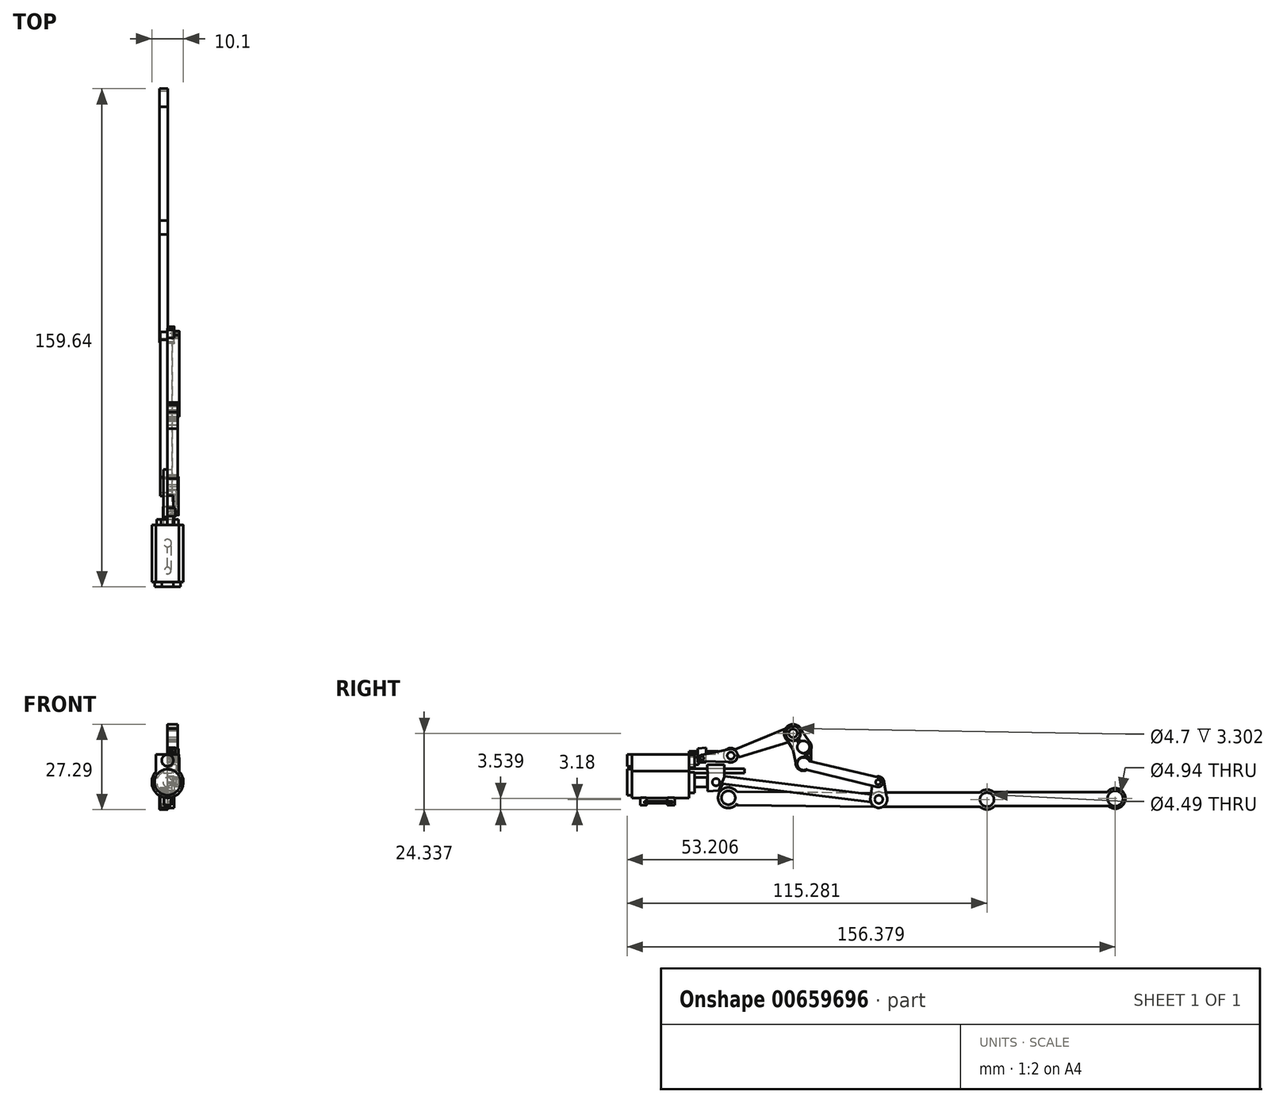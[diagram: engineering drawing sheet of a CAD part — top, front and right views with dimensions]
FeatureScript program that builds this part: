
annotation { "Feature Type Name" : "Feature", "Feature Type Description" : "" }
export const myFeature = defineFeature(function(context is Context, id is Id, definition is map)
    precondition{}
    {
        {
            var Q0;
            Q0=qCreatedBy(makeId("Front.planeOp"),FACE);
            var sketch = newSketch(context, id + "F0", { "sketchPlane" : qUnion([Q0])});
            skCircle(sketch, "E0", {"center": v(0, 0) * mm, "radius": 5.05 * mm});
            skLineSegment(sketch, "E1.bottom", {"start": v(-3.69, 8.87) * mm, "end": v(3.58, 8.87) * mm});
            skLineSegment(sketch, "E1.top", {"start": v(-3.69, 3.57) * mm, "end": v(3.58, 3.57) * mm});
            skLineSegment(sketch, "E1.left", {"start": v(-3.69, 8.87) * mm, "end": v(-3.69, 3.57) * mm});
            skLineSegment(sketch, "E1.right", {"start": v(3.58, 8.87) * mm, "end": v(3.58, 3.57) * mm});
            skSolve(sketch);
        }
        {
            var Q0;
            Q0=qSketchRegion(id+"F0",true);
            extrude(context, id + "F1", {"entities" : qUnion([Q0]), "depth" : 18.29 * mm, "offsetDistance" : 25.4 * mm});
        }
        {
            var Q0;
            Q0=qCreatedBy(makeId("Front.planeOp"),FACE);
            var sketch = newSketch(context, id + "F2", { "sketchPlane" : qUnion([Q0])});
            skCircle(sketch, "E2", {"center": v(0, 0) * mm, "radius": 3.48 * mm});
            skCircle(sketch, "E3", {"center": v(0, 6.69) * mm, "radius": 2.05 * mm});
            skSolve(sketch);
        }
        {
            var Q0;
            Q0=qSketchRegion(id+"F2",true);
            extrude(context, id + "F3", {"entities" : qUnion([Q0]), "operationType" : NewBodyOperationType.ADD, "oppositeDirection" : true, "depth" : 1.78 * mm, "offsetDistance" : 25.4 * mm});
        }
        {
            var Q0;
            Q0=qCreatedBy(makeId("Front.planeOp"),FACE);
            var sketch = newSketch(context, id + "F4", { "sketchPlane" : qUnion([Q0])});
            skCircle(sketch, "E4", {"center": v(0, 0) * mm, "radius": 4.19 * mm});
            skCircle(sketch, "E5", {"center": v(0, 6.96) * mm, "radius": 1.86 * mm});
            skSolve(sketch);
        }
        {
            var Q0;
            Q0=qSketchRegion(id+"F4",true);
            extrude(context, id + "F5", {"entities" : qUnion([Q0]), "operationType" : NewBodyOperationType.ADD, "depth" : 19.8 * mm, "offsetDistance" : 25.4 * mm});
        }
        {
            var Q0;
            Q0=qCreatedBy(makeId("Top.planeOp"),FACE);
            var sketch = newSketch(context, id + "F6", { "sketchPlane" : qUnion([Q0])});
            skCircle(sketch, "E6", {"center": v(0, -14.6) * mm, "radius": 1.06 * mm});
            skCircle(sketch, "E7", {"center": v(0, -5.8) * mm, "radius": 1.24 * mm});
            skSolve(sketch);
        }
        {
            var Q0;
            Q0=qSketchRegion(id+"F6",true);
            extrude(context, id + "F7", {"entities" : qUnion([Q0]), "operationType" : NewBodyOperationType.ADD, "oppositeDirection" : true, "depth" : 7.37 * mm, "offsetDistance" : 25.4 * mm});
        }
        {
            var Q0;
            Q0=qCreatedBy(makeId("Right.planeOp"),FACE);
            var sketch = newSketch(context, id + "F8", { "sketchPlane" : qUnion([Q0])});
            skLineSegment(sketch, "E8.bottom", {"start": v(-14.36, -6.78) * mm, "end": v(-5.2, -6.78) * mm});
            skLineSegment(sketch, "E8.top", {"start": v(-14.36, -6.08) * mm, "end": v(-5.2, -6.08) * mm});
            skLineSegment(sketch, "E8.left", {"start": v(-14.36, -6.78) * mm, "end": v(-14.36, -6.08) * mm});
            skLineSegment(sketch, "E8.right", {"start": v(-5.2, -6.78) * mm, "end": v(-5.2, -6.08) * mm});
            skSolve(sketch);
        }
        {
            var Q0;
            Q0=qSketchRegion(id+"F8",true);
            extrude(context, id + "F9", {"entities" : qUnion([Q0]), "operationType" : NewBodyOperationType.ADD, "depth" : 1.27 * mm, "offsetDistance" : 25.4 * mm});
        }
        {
            var Q0;
            Q0=qCreatedBy(makeId("Front.planeOp"),FACE);
            var sketch = newSketch(context, id + "F10", { "sketchPlane" : qUnion([Q0])});
            skLineSegment(sketch, "E9.bottom", {"start": v(-1.32, 4.33) * mm, "end": v(1.32, 4.33) * mm});
            skLineSegment(sketch, "E9.top", {"start": v(-1.32, 2.91) * mm, "end": v(1.32, 2.91) * mm});
            skLineSegment(sketch, "E9.left", {"start": v(-1.32, 4.33) * mm, "end": v(-1.32, 2.91) * mm});
            skLineSegment(sketch, "E9.right", {"start": v(1.32, 4.33) * mm, "end": v(1.32, 2.91) * mm});
            skPoint(sketch, "E9.middle", {"position": v(0, 3.62) * mm});
            skSolve(sketch);
        }
        {
            var Q0;
            Q0=qSketchRegion(id+"F10",true);
            extrude(context, id + "F11", {"entities" : qUnion([Q0]), "operationType" : NewBodyOperationType.ADD, "oppositeDirection" : true, "depth" : 17.78 * mm, "offsetDistance" : 25.4 * mm});
        }
        {
            var Q0;
            Q0=qCreatedBy(makeId("Right.planeOp"),FACE);
            var sketch = newSketch(context, id + "F12", { "sketchPlane" : qUnion([Q0])});
            skLineSegment(sketch, "E10", {"start": v(5.85, 5.6) * mm, "end": v(11.32, 5.6) * mm});
            skLineSegment(sketch, "E11", {"start": v(11.32, 5.6) * mm, "end": v(11.32, 1.7) * mm});
            skLineSegment(sketch, "E12", {"start": v(11.32, 1.7) * mm, "end": v(6.02, 1.7) * mm});
            skLineSegment(sketch, "E13", {"start": v(6.02, 1.7) * mm, "end": v(5.85, 5.6) * mm});
            skLineSegment(sketch, "E14", {"start": v(6.02, 1.7) * mm, "end": v(6.02, -2.89) * mm});
            skLineSegment(sketch, "E15", {"start": v(11.32, 1.7) * mm, "end": v(9.55, -2.71) * mm});
            skLineSegment(sketch, "E16", {"start": v(9.55, -2.71) * mm, "end": v(6.02, -2.89) * mm});
            skCircle(sketch, "E17", {"center": v(8.67, 0) * mm, "radius": 1.18 * mm});
            skPoint(sketch, "E17.centerSnap0", {"position": v(8.67, 1.7) * mm});
            skSolve(sketch);
        }
        {
            var Q0;
            Q0=qSketchRegion(id+"F12",true);
            extrude(context, id + "F13", {"entities" : qUnion([Q0]), "operationType" : NewBodyOperationType.ADD, "depth" : 2.8 * mm, "offsetDistance" : 25.4 * mm});
        }
        {
            var Q0;
            Q0=qCreatedBy(makeId("Front.planeOp"),FACE);
            var sketch = newSketch(context, id + "F14", { "sketchPlane" : qUnion([Q0])});
            skCircle(sketch, "E18", {"center": v(0, 0) * mm, "radius": 1.49 * mm});
            skSolve(sketch);
        }
        {
            var Q0;
            Q0=qSketchRegion(id+"F14",true);
            extrude(context, id + "F15", {"entities" : qUnion([Q0]), "operationType" : NewBodyOperationType.ADD, "oppositeDirection" : true, "depth" : 5.84 * mm, "offsetDistance" : 25.4 * mm});
        }
        {
            var Q0;
            Q0=qCreatedBy(makeId("Right.planeOp"),FACE);
            var sketch = newSketch(context, id + "F16", { "sketchPlane" : qUnion([Q0])});
            skCircle(sketch, "E19", {"center": v(8.62, 0) * mm, "radius": 2.28 * mm});
            skLineSegment(sketch, "E20", {"start": v(8.62, 2.28) * mm, "end": v(58.69, -3.97) * mm});
            skLineSegment(sketch, "E21", {"start": v(58.69, -3.97) * mm, "end": v(58.38, -6.43) * mm});
            skLineSegment(sketch, "E22", {"start": v(58.38, -6.43) * mm, "end": v(8.62, -0.22) * mm});
            skLineSegment(sketch, "E23", {"start": v(8.62, -0.22) * mm, "end": v(58.38, -6.43) * mm});
            skCircle(sketch, "E24", {"center": v(60.87, -5.6) * mm, "radius": 2.52 * mm});
            skSolve(sketch);
        }
        {
            var Q0;
            Q0=qSketchRegion(id+"F16",true);
            extrude(context, id + "F17", {"entities" : qUnion([Q0]), "operationType" : NewBodyOperationType.ADD, "depth" : 1.52 * mm, "offsetDistance" : 25.4 * mm});
        }
        {
            var Q0;
            Q0=qCreatedBy(makeId("Right.planeOp"),FACE);
            var sketch = newSketch(context, id + "F18", { "sketchPlane" : qUnion([Q0])});
            skCircle(sketch, "E25", {"center": v(60.8, -5.52) * mm, "radius": 2.72 * mm});
            skCircle(sketch, "E26", {"center": v(60.66, 0) * mm, "radius": 1.84 * mm});
            skLineSegment(sketch, "E27", {"start": v(58.82, 0) * mm, "end": v(58.19, -4.77) * mm});
            skLineSegment(sketch, "E28", {"start": v(62.5, 0) * mm, "end": v(63.25, -4.3) * mm});
            skCircle(sketch, "E29", {"center": v(60.66, 0) * mm, "radius": 1.1 * mm});
            skCircle(sketch, "E30", {"center": v(60.8, -5.52) * mm, "radius": 1.3 * mm});
            skSolve(sketch);
        }
        {
            var Q0;
            Q0=qSketchRegion(id+"F18",true);
            extrude(context, id + "F19", {"entities" : qUnion([Q0]), "operationType" : NewBodyOperationType.ADD, "depth" : 2.16 * mm, "offsetDistance" : 25.4 * mm});
        }
        {
            var Q0;
            Q0=qCreatedBy(makeId("Right.planeOp"),FACE);
            var sketch = newSketch(context, id + "F20", { "sketchPlane" : qUnion([Q0])});
            skCircle(sketch, "E31", {"center": v(60.6, 0) * mm, "radius": 1.56 * mm});
            skCircle(sketch, "E32", {"center": v(60.6, 0) * mm, "radius": 0.82 * mm});
            skLineSegment(sketch, "E33", {"start": v(61.05, 1.5) * mm, "end": v(38.5, 6.7) * mm});
            skLineSegment(sketch, "E34", {"start": v(60.3, -1.53) * mm, "end": v(37.9, 3.97) * mm});
            skLineSegment(sketch, "E35", {"start": v(37.9, 3.97) * mm, "end": v(38.5, 6.7) * mm});
            skCircle(sketch, "E36", {"center": v(36.73, 5.88) * mm, "radius": 2.03 * mm});
            skSolve(sketch);
        }
        {
            var Q0;
            Q0=qSketchRegion(id+"F20",true);
            extrude(context, id + "F21", {"entities" : qUnion([Q0]), "operationType" : NewBodyOperationType.ADD, "depth" : 3.7 * mm, "offsetDistance" : 25.4 * mm});
        }
        {
            var Q0;
            Q0=qCreatedBy(makeId("Right.planeOp"),FACE);
            var sketch = newSketch(context, id + "F22", { "sketchPlane" : qUnion([Q0])});
            skCircle(sketch, "E37", {"center": v(36.65, 6.15) * mm, "radius": 2.53 * mm});
            skCircle(sketch, "E38", {"center": v(36.65, 11.27) * mm, "radius": 2.61 * mm});
            skCircle(sketch, "E39", {"center": v(33.4, 15.58) * mm, "radius": 2.95 * mm});
            skLineSegment(sketch, "E40", {"start": v(30.5, 15.03) * mm, "end": v(33.31, 10.53) * mm});
            skLineSegment(sketch, "E41", {"start": v(33.31, 10.53) * mm, "end": v(34.13, 6.4) * mm});
            skLineSegment(sketch, "E42", {"start": v(35.06, 18.01) * mm, "end": v(39, 12.43) * mm});
            skLineSegment(sketch, "E43", {"start": v(39, 12.43) * mm, "end": v(39.18, 6.4) * mm});
            skLineSegment(sketch, "E44", {"start": v(39.18, 11.93) * mm, "end": v(39.18, 6.4) * mm});
            skLineSegment(sketch, "E45", {"start": v(39.18, 11.34) * mm, "end": v(39.18, 6.4) * mm});
            skCircle(sketch, "E46", {"center": v(33.4, 15.58) * mm, "radius": 2.35 * mm});
            skCircle(sketch, "E47", {"center": v(36.65, 11.27) * mm, "radius": 1.96 * mm});
            skCircle(sketch, "E48", {"center": v(36.65, 6.15) * mm, "radius": 1.92 * mm});
            skSolve(sketch);
        }
        {
            var Q0;
            Q0=qSketchRegion(id+"F22",true);
            extrude(context, id + "F23", {"entities" : qUnion([Q0]), "operationType" : NewBodyOperationType.ADD, "depth" : 3.3 * mm, "offsetDistance" : 25.4 * mm});
        }
        {
            var Q0;
            Q0=qCreatedBy(makeId("Right.planeOp"),FACE);
            var sketch = newSketch(context, id + "F24", { "sketchPlane" : qUnion([Q0])});
            skCircle(sketch, "E49", {"center": v(33.33, 15.68) * mm, "radius": 2.3 * mm});
            skCircle(sketch, "E50", {"center": v(33.33, 15.68) * mm, "radius": 1.36 * mm});
            skLineSegment(sketch, "E51", {"start": v(33.02, 17.97) * mm, "end": v(14.86, 10.58) * mm});
            skLineSegment(sketch, "E52", {"start": v(34.43, 13.65) * mm, "end": v(15.98, 7.96) * mm});
            skLineSegment(sketch, "E53", {"start": v(15.98, 7.96) * mm, "end": v(14.86, 10.58) * mm});
            skCircle(sketch, "E54", {"center": v(13.35, 8.6) * mm, "radius": 2.32 * mm});
            skSolve(sketch);
        }
        {
            var Q0;
            Q0=qSketchRegion(id+"F24",true);
            extrude(context, id + "F25", {"entities" : qUnion([Q0]), "operationType" : NewBodyOperationType.ADD, "depth" : 3.25 * mm, "offsetDistance" : 25.4 * mm});
        }
        {
            var Q0;
            Q0=qCreatedBy(makeId("Right.planeOp"),FACE);
            var sketch = newSketch(context, id + "F26", { "sketchPlane" : qUnion([Q0])});
            skLineSegment(sketch, "E55.bottom", {"start": v(0, 8.97) * mm, "end": v(9.4, 8.97) * mm});
            skLineSegment(sketch, "E55.top", {"start": v(0, 9.85) * mm, "end": v(9.4, 9.85) * mm});
            skLineSegment(sketch, "E55.left", {"start": v(0, 8.97) * mm, "end": v(0, 9.85) * mm});
            skLineSegment(sketch, "E55.right", {"start": v(9.4, 8.97) * mm, "end": v(9.4, 9.85) * mm});
            skSolve(sketch);
        }
        {
            var Q0;
            Q0=qSketchRegion(id+"F26",true);
            extrude(context, id + "F27", {"entities" : qUnion([Q0]), "depth" : 1.88 * mm, "offsetDistance" : 25.4 * mm});
        }
        {
            var Q0;
            Q0=qCreatedBy(makeId("Right.planeOp"),FACE);
            var sketch = newSketch(context, id + "F28", { "sketchPlane" : qUnion([Q0])});
            skLineSegment(sketch, "E56", {"start": v(2.86, 10.74) * mm, "end": v(2.86, 6.36) * mm});
            skLineSegment(sketch, "E57", {"start": v(2.86, 6.36) * mm, "end": v(5.49, 6.36) * mm});
            skLineSegment(sketch, "E58", {"start": v(5.49, 6.36) * mm, "end": v(5.49, 10.98) * mm});
            skLineSegment(sketch, "E59", {"start": v(5.49, 10.98) * mm, "end": v(2.86, 10.74) * mm});
            skCircle(sketch, "E60", {"center": v(4.13, 7.8) * mm, "radius": 1.35 * mm});
            skSolve(sketch);
        }
        {
            var Q0;
            Q0=qSketchRegion(id+"F28",true);
            extrude(context, id + "F29", {"entities" : qUnion([Q0]), "operationType" : NewBodyOperationType.ADD, "depth" : 2.54 * mm, "offsetDistance" : 25.4 * mm});
        }
        {
            var Q0;
            Q0=qCreatedBy(makeId("Front.planeOp"),FACE);
            var sketch = newSketch(context, id + "F30", { "sketchPlane" : qUnion([Q0])});
            skCircle(sketch, "E61", {"center": v(0.78, 6.76) * mm, "radius": 1.2 * mm});
            skSolve(sketch);
        }
        {
            var Q0;
            Q0=qSketchRegion(id+"F30",true);
            extrude(context, id + "F31", {"entities" : qUnion([Q0]), "oppositeDirection" : true, "depth" : 3 * mm, "offsetDistance" : 25.4 * mm});
        }
        {
            var Q0;
            Q0=qCreatedBy(makeId("Right.planeOp"),FACE);
            var sketch = newSketch(context, id + "F32", { "sketchPlane" : qUnion([Q0])});
            skCircle(sketch, "E62", {"center": v(13.41, 8.5) * mm, "radius": 2.14 * mm});
            skCircle(sketch, "E63", {"center": v(13.41, 8.5) * mm, "radius": 1.15 * mm});
            skCircle(sketch, "E64", {"center": v(4.18, 7.72) * mm, "radius": 1.01 * mm});
            skLineSegment(sketch, "E65", {"start": v(12.84, 10.57) * mm, "end": v(4.18, 8.73) * mm});
            skLineSegment(sketch, "E66", {"start": v(13.85, 6.41) * mm, "end": v(4.18, 6.7) * mm});
            skCircle(sketch, "E67", {"center": v(4.18, 7.72) * mm, "radius": 0.57 * mm});
            skLineSegment(sketch, "E68", {"start": v(4.18, 8.73) * mm, "end": v(4.18, 6.7) * mm});
            skSolve(sketch);
        }
        {
            var Q0;
            Q0=qSketchRegion(id+"F32",true);
            extrude(context, id + "F33", {"entities" : qUnion([Q0]), "depth" : 3.56 * mm, "offsetDistance" : 25.4 * mm});
        }
        {
            var Q0;
            Q0=qCreatedBy(makeId("Right.planeOp"),FACE);
            var sketch = newSketch(context, id + "F34", { "sketchPlane" : qUnion([Q0])});
            skCircle(sketch, "E69", {"center": v(60.8, -5.59) * mm, "radius": 2.5 * mm});
            skCircle(sketch, "E70", {"center": v(60.8, -5.59) * mm, "radius": 1.34 * mm});
            skLineSegment(sketch, "E71", {"start": v(59.33, -3.58) * mm, "end": v(15.4, -3.02) * mm});
            skLineSegment(sketch, "E72", {"start": v(59.86, -7.9) * mm, "end": v(15.4, -7.34) * mm});
            skLineSegment(sketch, "E73", {"start": v(15.4, -7.34) * mm, "end": v(15.4, -3.02) * mm});
            skCircle(sketch, "E74", {"center": v(12.62, -5) * mm, "radius": 3.31 * mm});
            skCircle(sketch, "E75", {"center": v(12.62, -5) * mm, "radius": 2.21 * mm});
            skSolve(sketch);
        }
        {
            var Q0;
            Q0 = qSketchRegion(id + "F34", true);
            extrude(context, id + "F35", {"entities" : qUnion([Q0]), "operationType" : NewBodyOperationType.ADD, "oppositeDirection" : true, "depth" : 2.3 * mm, "offsetDistance" : 25.4 * mm});
        }
        {
            var Q0;
            Q0=qCreatedBy(makeId("Right.planeOp"),FACE);
            var sketch = newSketch(context, id + "F36", { "sketchPlane" : qUnion([Q0])});
            skCircle(sketch, "E76", {"center": v(60.84, -5.6) * mm, "radius": 2.41 * mm});
            skCircle(sketch, "E77", {"center": v(60.84, -5.6) * mm, "radius": 1.25 * mm});
            skLineSegment(sketch, "E78", {"start": v(61.62, -3.32) * mm, "end": v(93.13, -3.32) * mm});
            skLineSegment(sketch, "E79", {"start": v(61.55, -7.9) * mm, "end": v(93.13, -7.9) * mm});
            skLineSegment(sketch, "E80", {"start": v(93.13, -7.9) * mm, "end": v(93.13, -3.32) * mm});
            skCircle(sketch, "E81", {"center": v(95.47, -5.58) * mm, "radius": 3.18 * mm});
            skLineSegment(sketch, "E82", {"start": v(97.53, -3.15) * mm, "end": v(134.1, -3.15) * mm});
            skLineSegment(sketch, "E83", {"start": v(97.86, -7.69) * mm, "end": v(134.1, -7.69) * mm});
            skLineSegment(sketch, "E84", {"start": v(134.1, -7.69) * mm, "end": v(134.1, -3.15) * mm});
            skCircle(sketch, "E85", {"center": v(136.57, -5.22) * mm, "radius": 3.27 * mm});
            skCircle(sketch, "E86", {"center": v(95.47, -5.58) * mm, "radius": 2.25 * mm});
            skCircle(sketch, "E87", {"center": v(136.57, -5.22) * mm, "radius": 2.47 * mm});
            skSolve(sketch);
        }
        {
            var Q0;
            Q0 = qSketchRegion(id + "F36", true);
            extrude(context, id + "F37", {"entities" : qUnion([Q0]), "operationType" : NewBodyOperationType.ADD, "oppositeDirection" : true, "depth" : 2.54 * mm, "offsetDistance" : 25.4 * mm});
        }
        {
            var Q0;
            Q0 = qSketchRegion(id + "F36", true);
            extrude(context, id + "F38", {"entities" : qUnion([Q0]), "operationType" : NewBodyOperationType.ADD, "depth" : 0.05 * mm, "offsetDistance" : 25.4 * mm});
        }
    });
